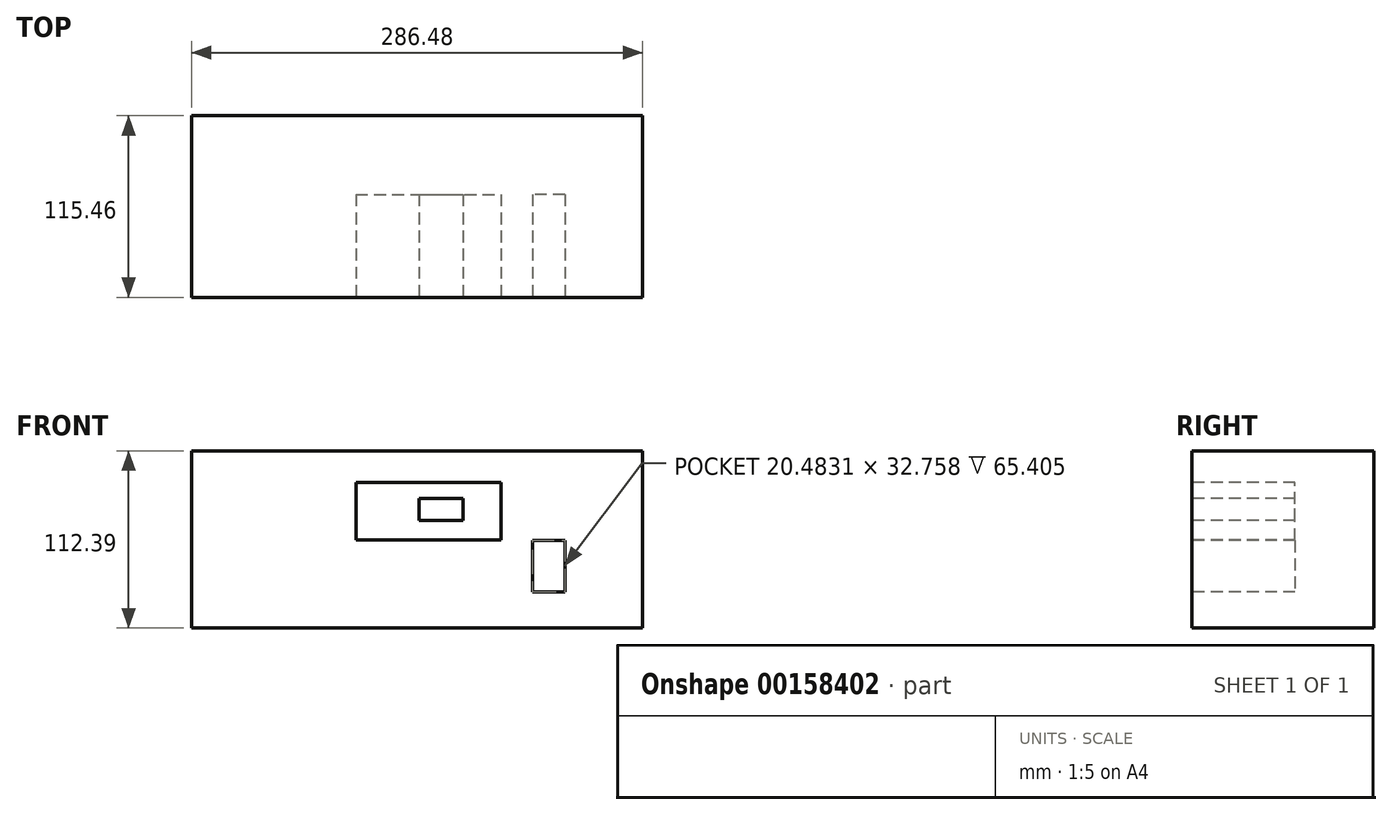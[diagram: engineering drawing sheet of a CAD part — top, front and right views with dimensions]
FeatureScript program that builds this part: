
annotation { "Feature Type Name" : "Feature", "Feature Type Description" : "" }
export const myFeature = defineFeature(function(context is Context, id is Id, definition is map)
    precondition{}
    {
        {
            var Q0;
            Q0=qCreatedBy(makeId("Top.planeOp"),FACE);
            var sketch = newSketch(context, id + "F0", { "sketchPlane" : qUnion([Q0])});
            skLineSegment(sketch, "E0.bottom", {"start": v(0, -57.9) * mm, "end": v(-61.69, -57.9) * mm});
            skLineSegment(sketch, "E0.top", {"start": v(0, 57.56) * mm, "end": v(-61.69, 57.56) * mm});
            skLineSegment(sketch, "E0.left", {"start": v(0, -57.9) * mm, "end": v(0, 57.56) * mm});
            skLineSegment(sketch, "E0.right", {"start": v(-61.69, -57.9) * mm, "end": v(-61.69, 57.56) * mm});
            skSolve(sketch);
        }
        {
            var Q0;
            Q0=makeQuery(id+"F0.imprint","IMPRINT",FACE,{"disambiguationData":[TD([[makeQuery(id+"F0.imprint","IMPRINT",EDGE,{"derivedFrom":sQuery(id+"F0.wireOp",EDGE,"E0.bottom")}),-1.0]])]});
            extrude(context, id + "F1", {"entities" : qUnion([Q0]), "depth" : 112.4 * mm});
        }
        {
            var Q0;
            Q0=makeQuery(id+"F1.opExtrude","SWEPT_FACE",FACE,{"disambiguationData":[OSD([sQuery(id+"F0.wireOp",EDGE,"E0.left")])]});
            extrude(context, id + "F2", {"entities" : qUnion([Q0]), "operationType" : NewBodyOperationType.ADD, "depth" : 224.79 * mm});
        }
        {
            var Q0;
            {var subQ0=sQuery(id+"F0.wireOp",EDGE,"E0.bottom");Q0=makeQuery(id+"F2.boolean.opBoolean","MERGE",FACE,{"derivedFrom":[makeQuery(id+"F1.opExtrude","SWEPT_FACE",FACE,{"disambiguationData":[OSD([subQ0])]}),makeQuery(id+"F2.opExtrude","SWEPT_FACE",FACE,{"disambiguationData":[OSD([subQ0,sQuery(id+"F0.wireOp",EDGE,"E0.left")])]})]});}
            var sketch = newSketch(context, id + "F3", { "sketchPlane" : qUnion([Q0])});
            skLineSegment(sketch, "E1.bottom", {"start": v(42.76, 55.73) * mm, "end": v(134.72, 55.73) * mm});
            skLineSegment(sketch, "E1.top", {"start": v(42.76, 92.47) * mm, "end": v(134.72, 92.47) * mm});
            skLineSegment(sketch, "E1.left", {"start": v(42.76, 55.73) * mm, "end": v(42.76, 92.47) * mm});
            skLineSegment(sketch, "E1.right", {"start": v(134.72, 55.73) * mm, "end": v(134.72, 92.47) * mm});
            skLineSegment(sketch, "E2.bottom", {"start": v(175.39, 55.56) * mm, "end": v(154.9, 55.56) * mm});
            skLineSegment(sketch, "E2.top", {"start": v(175.39, 22.8) * mm, "end": v(154.9, 22.8) * mm});
            skLineSegment(sketch, "E2.left", {"start": v(175.39, 55.56) * mm, "end": v(175.39, 22.8) * mm});
            skLineSegment(sketch, "E2.right", {"start": v(154.9, 55.56) * mm, "end": v(154.9, 22.8) * mm});
            skLineSegment(sketch, "E3.bottom", {"start": v(82.85, 68.27) * mm, "end": v(110.6, 68.27) * mm});
            skLineSegment(sketch, "E3.top", {"start": v(82.85, 82.12) * mm, "end": v(110.6, 82.12) * mm});
            skLineSegment(sketch, "E3.left", {"start": v(82.85, 68.27) * mm, "end": v(82.85, 82.12) * mm});
            skLineSegment(sketch, "E3.right", {"start": v(110.6, 68.27) * mm, "end": v(110.6, 82.12) * mm});
            skSolve(sketch);
        }
        {
            var Q0;
            Q0=makeQuery(id+"F3.imprint","IMPRINT",FACE,{"disambiguationData":[TD([[makeQuery(id+"F3.imprint","IMPRINT",EDGE,{"derivedFrom":sQuery(id+"F3.wireOp",EDGE,"E1.bottom")}),1.0]])]});
            var Q1;
            Q1=makeQuery(id+"F3.imprint","IMPRINT",FACE,{"disambiguationData":[TD([[makeQuery(id+"F3.imprint","IMPRINT",EDGE,{"derivedFrom":sQuery(id+"F3.wireOp",EDGE,"E2.bottom")}),1.0]])]});
            extrude(context, id + "F4", {"entities" : qUnion([Q0, Q1]), "operationType" : NewBodyOperationType.REMOVE, "oppositeDirection" : true, "depth" : 65.4 * mm});
        }
    });
